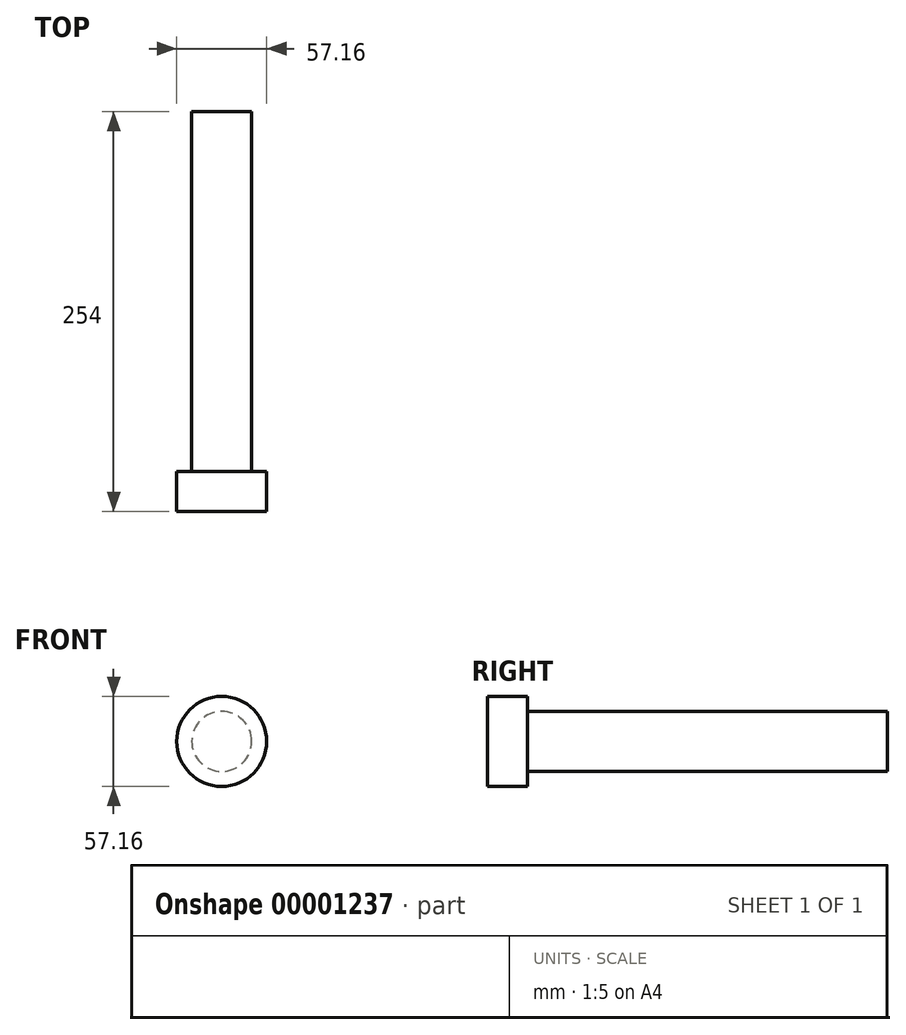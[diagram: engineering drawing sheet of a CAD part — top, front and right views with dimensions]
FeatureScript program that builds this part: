
annotation { "Feature Type Name" : "Feature", "Feature Type Description" : "" }
export const myFeature = defineFeature(function(context is Context, id is Id, definition is map)
    precondition{}
    {
        {
            var Q0;
            Q0=qCreatedBy(makeId("Front.planeOp"),FACE);
            var sketch = newSketch(context, id + "F0", { "sketchPlane" : qUnion([Q0])});
            skCircle(sketch, "E0", {"center": v(0, 0) * mm, "radius": 19.05 * mm});
            skSolve(sketch);
        }
        {
            var Q0;
            Q0=makeQuery(id+"F0.imprint","IMPRINT",FACE,{"disambiguationData":[TD([[makeQuery(id+"F0.imprint","IMPRINT",EDGE,{"derivedFrom":sQuery(id+"F0.wireOp",EDGE,"E0")}),1.0]])]});
            extrude(context, id + "F1", {"entities" : qUnion([Q0]), "depth" : 254 * mm});
        }
        {
            var Q0;
            Q0=makeQuery(id+"F1.opExtrude","CAP_FACE",FACE,{"disambiguationData":[OSD([sQuery(id+"F0.wireOp",EDGE,"E0")])],"isStart":false});
            var sketch = newSketch(context, id + "F2", { "sketchPlane" : qUnion([Q0])});
            skCircle(sketch, "E1", {"center": v(0, 0) * mm, "radius": 28.58 * mm});
            skSolve(sketch);
        }
        {
            var Q0;
            Q0=makeQuery(id+"F2.imprint","IMPRINT",FACE,{"disambiguationData":[TD([[makeQuery(id+"F2.imprint","IMPRINT",EDGE,{"derivedFrom":sQuery(id+"F2.wireOp",EDGE,"E1")}),1.0]])]});
            extrude(context, id + "F3", {"entities" : qUnion([Q0]), "operationType" : NewBodyOperationType.ADD, "oppositeDirection" : true, "depth" : 25.4 * mm});
        }
    });
